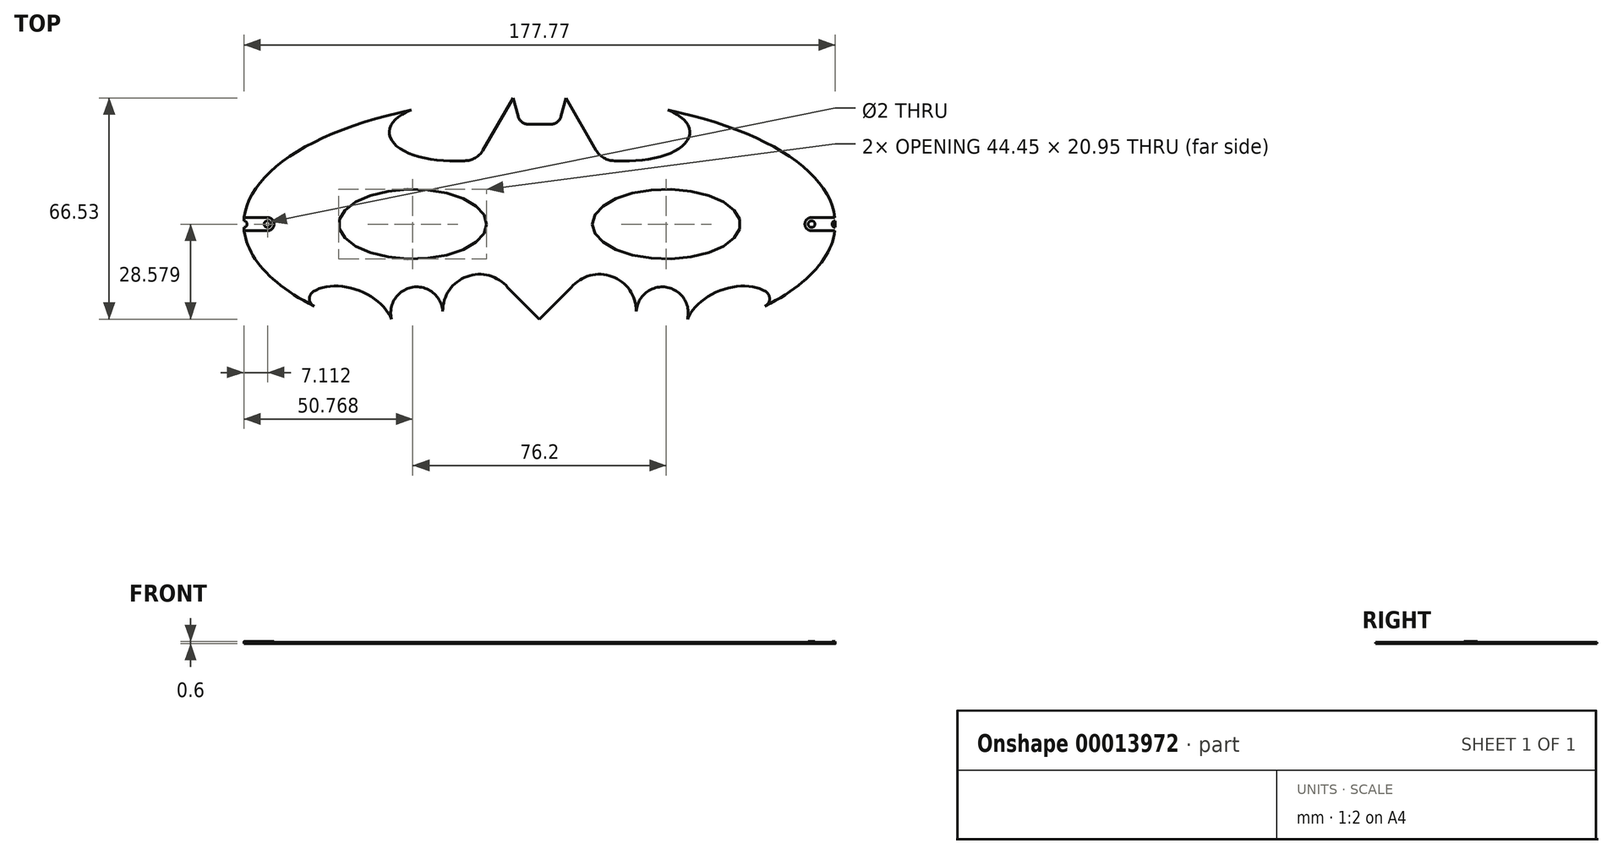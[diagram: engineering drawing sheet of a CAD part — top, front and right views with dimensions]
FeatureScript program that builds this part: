
annotation { "Feature Type Name" : "Feature", "Feature Type Description" : "" }
export const myFeature = defineFeature(function(context is Context, id is Id, definition is map)
    precondition{}
    {
        {
            var Q0;
            Q0=qCreatedBy(makeId("Top.planeOp"),FACE);
            var sketch = newSketch(context, id + "F0", { "sketchPlane" : qUnion([Q0])});
            skEllipse(sketch, "E0", {"center": v(-79.2, 13.69) * mm, "majorRadius": 22.23 * mm, "minorRadius": 10.48 * mm, "majorAxis": v(1, 0)});
            skLineSegment(sketch, "E1", {"start": v(-79.2, 13.69) * mm, "end": v(-41.1, 13.69) * mm, "construction": true});
            skLineSegment(sketch, "E2", {"start": v(-41.1, 13.69) * mm, "end": v(-41.1, 51.79) * mm, "construction": true});
            skLineSegment(sketch, "E3", {"start": v(-41.1, 13.69) * mm, "end": v(-41.1, -24.41) * mm, "construction": true});
            skEllipticalArc(sketch, "E4", {});
            skLineSegment(sketch, "E5", {"start": v(-63.62, 32.74) * mm, "end": v(-68.09, 32.74) * mm});
            skLineSegment(sketch, "E6", {"start": v(-44.49, 43.73) * mm, "end": v(-41.1, 43.73) * mm});
            skLineSegment(sketch, "E7", {"start": v(-41.1, 13.69) * mm, "end": v(-56.98, 13.69) * mm, "construction": true});
            skLineSegment(sketch, "E8", {"start": v(-49.04, 13.69) * mm, "end": v(-49.04, 51.64) * mm, "construction": true});
            skLineSegment(sketch, "E9", {"start": v(-49.04, 51.64) * mm, "end": v(-47.55, 46.09) * mm});
            skArc(sketch, "E10.filletArc", {"start": v(-47.55, 46.09) * mm, "mid": v(-46.42, 44.39) * mm, "end": v(-44.49, 43.73) * mm});
            skLineSegment(sketch, "E11", {"start": v(-49.04, 51.64) * mm, "end": v(-58.12, 35.91) * mm});
            skPoint(sketch, "E12.newPointA", {"position": v(-41.1, 32.74) * mm});
            skArc(sketch, "E12.filletArc", {"start": v(-63.62, 32.74) * mm, "mid": v(-60.44, 33.6) * mm, "end": v(-58.12, 35.91) * mm});
            skLineSegment(sketch, "E13", {"start": v(-56.98, 13.69) * mm, "end": v(-79.2, 13.69) * mm, "construction": true});
            skLineSegment(sketch, "E14", {"start": v(-68.09, 13.69) * mm, "end": v(-68.09, 50) * mm, "construction": true});
            skLineSegment(sketch, "E15", {"start": v(-68.09, 32.74) * mm, "end": v(-68.09, 50) * mm, "construction": true});
            skEllipticalArc(sketch, "E16", {});
            skLineSegment(sketch, "E17", {"start": v(-41.1, 43.73) * mm, "end": v(-41.1, -24.41) * mm, "construction": true});
            skPoint(sketch, "E18.orphan", {"position": v(-3, 13.69) * mm});
            skLineSegment(sketch, "E19", {"start": v(-41.1, 13.69) * mm, "end": v(-41.1, -14.89) * mm, "construction": true});
            skLineSegment(sketch, "E20", {"start": v(-41.1, -5.36) * mm, "end": v(-118.1, -5.36) * mm, "construction": true});
            skLineSegment(sketch, "E21", {"start": v(-41.1, -24.41) * mm, "end": v(-41.1, -5.36) * mm, "construction": true});
            skLineSegment(sketch, "E22", {"start": v(-79.2, 13.69) * mm, "end": v(-79.2, -20.73) * mm, "construction": true});
            skLineSegment(sketch, "E23", {"start": v(-79.2, -5.36) * mm, "end": v(-79.2, -20.73) * mm, "construction": true});
            skLineSegment(sketch, "E24", {"start": v(-79.2, -5.36) * mm, "end": v(-118.1, -5.36) * mm, "construction": true});
            skLineSegment(sketch, "E25", {"start": v(-98.65, -5.36) * mm, "end": v(-98.65, -15.35) * mm, "construction": true});
            skLineSegment(sketch, "E26", {"start": v(-79.2, -5.36) * mm, "end": v(-41.1, -5.36) * mm, "construction": true});
            skLineSegment(sketch, "E27", {"start": v(-60.15, -5.36) * mm, "end": v(-60.15, -23.53) * mm, "construction": true});
            skPoint(sketch, "E28.start.orphan", {"position": v(-41.1, -14.89) * mm});
            skLineSegment(sketch, "E29", {"start": v(-85.57, -14.89) * mm, "end": v(-85.61, -14.89) * mm});
            skPoint(sketch, "E30.orphan", {"position": v(-98.65, -14.89) * mm});
            skPoint(sketch, "E31.third.point", {"position": v(-101.98, -9.03) * mm});
            skLineSegment(sketch, "E32", {"start": v(-41.1, -14.89) * mm, "end": v(-50.63, -5.36) * mm});
            skArc(sketch, "E33", {"start": v(-50.63, -5.36) * mm, "mid": v(-62.9, -2.07) * mm, "end": v(-70.2, -12.49) * mm});
            skPoint(sketch, "E33.third.point", {"position": v(-69.11, -17.28) * mm});
            skLineSegment(sketch, "E34", {"start": v(-59.11, -12.49) * mm, "end": v(-70.2, -12.49) * mm, "construction": true});
            skArc(sketch, "E35", {"start": v(-70.2, -12.49) * mm, "mid": v(-79.46, -5.34) * mm, "end": v(-85.42, -15.4) * mm});
            skPoint(sketch, "E35.second.point", {"position": v(-85.57, -14.89) * mm});
            skPoint(sketch, "E35.third.point", {"position": v(-85.64, -14.58) * mm});
            skEllipticalArc(sketch, "E36", {});
            skArc(sketch, "E37.trimOffspring", {"start": v(-79.56, -20.66) * mm, "mid": v(-79.38, -20.7) * mm, "end": v(-79.2, -20.73) * mm});
            skEllipticalArc(sketch, "E38.trimOffspring", {});
            skArc(sketch, "E39", {"start": v(-109.08, -6.6) * mm, "mid": v(-110.26, -8.84) * mm, "end": v(-108.88, -10.97) * mm});
            skPoint(sketch, "E39.first.point", {"position": v(-109.08, -6.6) * mm});
            skPoint(sketch, "E39.second.point", {"position": v(-108.88, -10.97) * mm});
            skPoint(sketch, "E39.third.point", {"position": v(-105.79, -10.3) * mm});
            skEllipticalArc(sketch, "E40.0.MirrorCS", {});
            skArc(sketch, "E40.1.MirrorCS", {"start": v(-2.64, -20.66) * mm, "mid": v(-2.82, -20.7) * mm, "end": v(-3, -20.73) * mm});
            skArc(sketch, "E40.2.MirrorCS", {"start": v(-34.65, 46.09) * mm, "mid": v(-35.79, 44.39) * mm, "end": v(-37.72, 43.73) * mm});
            skLineSegment(sketch, "E40.3.MirrorCS", {"start": v(-37.72, 43.73) * mm, "end": v(-41.1, 43.73) * mm});
            skLineSegment(sketch, "E40.5.MirrorCS", {"start": v(-3, -5.36) * mm, "end": v(35.89, -5.36) * mm, "construction": true});
            skLineSegment(sketch, "E40.6.MirrorCS", {"start": v(-3, 13.69) * mm, "end": v(-41.1, 13.69) * mm, "construction": true});
            skLineSegment(sketch, "E40.7.MirrorCS", {"start": v(-3, -5.36) * mm, "end": v(-3, -20.73) * mm, "construction": true});
            skLineSegment(sketch, "E40.10.MirrorCS", {"start": v(-23.09, -12.49) * mm, "end": v(-12, -12.49) * mm, "construction": true});
            skPoint(sketch, "E40.11.MirrorP", {"position": v(-13.1, -17.28) * mm});
            skArc(sketch, "E40.12.MirrorCS", {"start": v(-31.58, -5.36) * mm, "mid": v(-19.3, -2.07) * mm, "end": v(-12, -12.49) * mm});
            skLineSegment(sketch, "E40.13.MirrorCS", {"start": v(-41.1, -5.36) * mm, "end": v(35.89, -5.36) * mm, "construction": true});
            skPoint(sketch, "E40.14.MirrorP", {"position": v(3.37, -14.89) * mm});
            skPoint(sketch, "E40.15.MirrorP", {"position": v(3.44, -14.58) * mm});
            skLineSegment(sketch, "E40.16.MirrorCS", {"start": v(-41.1, -14.89) * mm, "end": v(-31.58, -5.36) * mm});
            skEllipticalArc(sketch, "E40.17.MirrorCS", {});
            skEllipticalArc(sketch, "E40.18.MirrorCS", {});
            skLineSegment(sketch, "E40.20.MirrorCS", {"start": v(-3, -5.36) * mm, "end": v(-41.1, -5.36) * mm, "construction": true});
            skPoint(sketch, "E40.21.MirrorP", {"position": v(26.67, -10.97) * mm});
            skLineSegment(sketch, "E40.23.MirrorCS", {"start": v(-33.16, 51.64) * mm, "end": v(-24.09, 35.91) * mm});
            skArc(sketch, "E40.25.MirrorCS", {"start": v(26.88, -6.6) * mm, "mid": v(28.05, -8.84) * mm, "end": v(26.67, -10.97) * mm});
            skLineSegment(sketch, "E40.26.MirrorCS", {"start": v(-33.16, 13.69) * mm, "end": v(-33.16, 51.64) * mm, "construction": true});
            skPoint(sketch, "E40.27.MirrorP", {"position": v(23.58, -10.3) * mm});
            skLineSegment(sketch, "E40.28.MirrorCS", {"start": v(-3, 13.69) * mm, "end": v(-3, -20.73) * mm, "construction": true});
            skArc(sketch, "E40.29.MirrorCS", {"start": v(-18.59, 32.74) * mm, "mid": v(-21.76, 33.6) * mm, "end": v(-24.09, 35.91) * mm});
            skPoint(sketch, "E40.30.MirrorP", {"position": v(16.44, -14.89) * mm});
            skLineSegment(sketch, "E40.31.MirrorCS", {"start": v(-18.59, 32.74) * mm, "end": v(-14.11, 32.74) * mm});
            skLineSegment(sketch, "E40.32.MirrorCS", {"start": v(-14.11, 13.69) * mm, "end": v(-14.11, 50) * mm, "construction": true});
            skPoint(sketch, "E40.33.MirrorP", {"position": v(26.88, -6.6) * mm});
            skLineSegment(sketch, "E40.34.MirrorCS", {"start": v(-22.05, -5.36) * mm, "end": v(-22.05, -23.53) * mm, "construction": true});
            skLineSegment(sketch, "E40.35.MirrorCS", {"start": v(-41.1, 13.69) * mm, "end": v(-25.23, 13.69) * mm, "construction": true});
            skLineSegment(sketch, "E40.36.MirrorCS", {"start": v(-25.23, 13.69) * mm, "end": v(-3, 13.69) * mm, "construction": true});
            skPoint(sketch, "E40.37.MirrorP", {"position": v(19.77, -9.03) * mm});
            skLineSegment(sketch, "E40.38.MirrorCS", {"start": v(16.44, -5.36) * mm, "end": v(16.44, -15.35) * mm, "construction": true});
            skEllipse(sketch, "E40.39.MirrorC", {"center": v(-3, 13.69) * mm, "majorRadius": 22.23 * mm, "minorRadius": 10.48 * mm, "majorAxis": v(-1, 0)});
            skLineSegment(sketch, "E40.40.MirrorCS", {"start": v(-14.11, 32.74) * mm, "end": v(-14.11, 50) * mm, "construction": true});
            skLineSegment(sketch, "E40.41.MirrorCS", {"start": v(-33.16, 51.64) * mm, "end": v(-34.65, 46.09) * mm});
            skArc(sketch, "E40.42.MirrorCS", {"start": v(-12, -12.49) * mm, "mid": v(-2.74, -5.34) * mm, "end": v(3.22, -15.4) * mm});
            skEllipticalArc(sketch, "E40.43.MirrorCS", {});
            skEllipse(sketch, "E41.39.MirrorC", {"center": v(-3, 13.69) * mm, "majorRadius": 22.23 * mm, "minorRadius": 10.48 * mm, "majorAxis": v(-1, 0)});
            skEllipse(sketch, "E42.39.MirrorC", {"center": v(-3, 13.69) * mm, "majorRadius": 22.23 * mm, "minorRadius": 10.48 * mm, "majorAxis": v(-1, 0)});
            skLineSegment(sketch, "E43.2.MirrorCS", {"start": v(3.37, -14.89) * mm, "end": v(3.4, -14.89) * mm});
            skEllipse(sketch, "E43.40.MirrorC", {"center": v(-3, 13.69) * mm, "majorRadius": 22.23 * mm, "minorRadius": 10.48 * mm, "majorAxis": v(-1, 0)});
            const initialGuessF0  = {"E4": [-0.04110175946389499, 0.013689403422176838, -1, 0, 0.0889, 0.0381, 5.161492964245287, 0.7038030939227414], "E16": [-0.068089259463895, 0.041365408846871524, -1, 0, 0.018210322861197562, 0.008626005424694693, 5.403646126768505, 1.5707963267948966], "E36": [-0.0986465886621133, -0.014885596577823165, -0.9340282281485562, 0.35719920075732065, 0.014136312485541013, 0.009166058700018152, 3.6220749591931227, 5.829835207342765], "E38.trimOffspring": [-0.04110175946389499, 0.013689403422176838, -1, 0, 0.0889, 0.0381, 1.1233638688153285, 1.127885282721257], "E40.0.MirrorCS": [-0.04110175946389499, 0.013689403422176838, 1, 0, 0.0889, 0.0381, 5.155300024458329, 5.159821438364258], "E40.17.MirrorCS": [-0.04110175946389499, 0.013689403422176838, 1, 0, 0.0889, 0.0381, 5.579382213256845, 1.121692342934299], "E40.18.MirrorCS": [0.016443069734323315, -0.014885596577823165, 0.9340282281485562, 0.35719920075732065, 0.014136312485541013, 0.009166058700018152, 0.45335009983682095, 2.6611103479864635], "E40.43.MirrorCS": [-0.014114259463894982, 0.041365408846871524, 1, 0, 0.018210322861197562, 0.008626005424694693, 4.71238898038469, 0.879539180411081], "E40.0.MirrorCS": [-0.04110175946389499, 0.013689403422176838, 1, 0, 0.0889, 0.0381, 5.155300024458329, 5.159821438364258], "E40.17.MirrorCS": [-0.04110175946389499, 0.013689403422176838, 1, 0, 0.0889, 0.0381, 5.579382213256845, 1.121692342934299], "E40.18.MirrorCS": [0.016443069734323315, -0.014885596577823165, 0.9340282281485562, 0.35719920075732065, 0.014136312485541013, 0.009166058700018152, 0.45335009983682095, 2.6611103479864635], "E40.43.MirrorCS": [-0.014114259463894982, 0.041365408846871524, 1, 0, 0.018210322861197562, 0.008626005424694693, 4.71238898038469, 0.879539180411081], "E40.0.MirrorCS": [-0.04110175946389499, 0.013689403422176838, 1, 0, 0.0889, 0.0381, 5.155300024458329, 5.159821438364258], "E40.17.MirrorCS": [-0.04110175946389499, 0.013689403422176838, 1, 0, 0.0889, 0.0381, 5.579382213256845, 1.121692342934299], "E40.18.MirrorCS": [0.016443069734323315, -0.014885596577823165, 0.9340282281485562, 0.35719920075732065, 0.014136312485541013, 0.009166058700018152, 0.45335009983682095, 2.6611103479864635], "E40.43.MirrorCS": [-0.014114259463894982, 0.041365408846871524, 1, 0, 0.018210322861197562, 0.008626005424694693, 4.71238898038469, 0.879539180411081], "E40.43.MirrorCS": [-0.014114259463894982, 0.041365408846871524, 1, 0, 0.018210322861197562, 0.008626005424694693, 4.71238898038469, 0.879539180411081], "E40.17.MirrorCS": [-0.04110175946389499, 0.013689403422176838, 1, 0, 0.0889, 0.0381, 5.579382213256845, 1.121692342934299], "E40.0.MirrorCS": [-0.04110175946389499, 0.013689403422176838, 1, 0, 0.0889, 0.0381, 5.155300024458329, 5.159821438364258], "E40.17.MirrorCS": [-0.04110175946389499, 0.013689403422176838, 1, 0, 0.0889, 0.0381, 5.579382213256845, 1.121692342934299], "E40.18.MirrorCS": [0.016443069734323315, -0.014885596577823165, 0.9340282281485562, 0.35719920075732065, 0.014136312485541013, 0.009166058700018152, 0.45335009983682095, 2.6611103479864635], "E40.43.MirrorCS": [-0.014114259463894982, 0.041365408846871524, 1, 0, 0.018210322861197562, 0.008626005424694693, 4.71238898038469, 0.879539180411081]};
            skSetInitialGuess(sketch, initialGuessF0);
            skSolve(sketch);
        }
        {
            var Q0;
            Q0=makeQuery(id+"F0.imprint","IMPRINT",FACE,{"disambiguationData":[TD([[makeQuery(id+"F0.imprint","IMPRINT",EDGE,{"derivedFrom":sQuery(id+"F0.wireOp",EDGE,"E0")}),-1.0]])]});
            extrude(context, id + "F1", {"entities" : qUnion([Q0]), "depth" : .36 * mm});
        }
        {
            var Q0;
            Q0=makeQuery(id+"F1.opExtrude","CAP_FACE",FACE,{"disambiguationData":[OSD([sQuery(id+"F0.wireOp",EDGE,"E0"),sQuery(id+"F0.wireOp",EDGE,"E4"),sQuery(id+"F0.wireOp",EDGE,"E5"),sQuery(id+"F0.wireOp",EDGE,"E6"),sQuery(id+"F0.wireOp",EDGE,"E9"),sQuery(id+"F0.wireOp",EDGE,"E10.filletArc"),sQuery(id+"F0.wireOp",EDGE,"E11"),sQuery(id+"F0.wireOp",EDGE,"E12.filletArc"),sQuery(id+"F0.wireOp",EDGE,"E16"),sQuery(id+"F0.wireOp",EDGE,"E29"),sQuery(id+"F0.wireOp",EDGE,"E32"),sQuery(id+"F0.wireOp",EDGE,"E33"),sQuery(id+"F0.wireOp",EDGE,"E35"),sQuery(id+"F0.wireOp",EDGE,"E36"),sQuery(id+"F0.wireOp",EDGE,"E39"),sQuery(id+"F0.wireOp",EDGE,"E43.2.MirrorCS"),sQuery(id+"F0.wireOp",EDGE,"E40.3.MirrorCS"),sQuery(id+"F0.wireOp",EDGE,"E40.12.MirrorCS"),sQuery(id+"F0.wireOp",EDGE,"E40.16.MirrorCS"),sQuery(id+"F0.wireOp",EDGE,"E40.17.MirrorCS"),sQuery(id+"F0.wireOp",EDGE,"E40.2.MirrorCS"),sQuery(id+"F0.wireOp",EDGE,"E40.18.MirrorCS"),sQuery(id+"F0.wireOp",EDGE,"E40.23.MirrorCS"),sQuery(id+"F0.wireOp",EDGE,"E40.25.MirrorCS"),sQuery(id+"F0.wireOp",EDGE,"E40.29.MirrorCS"),sQuery(id+"F0.wireOp",EDGE,"E40.31.MirrorCS"),sQuery(id+"F0.wireOp",EDGE,"E43.40.MirrorC"),sQuery(id+"F0.wireOp",EDGE,"E40.41.MirrorCS"),sQuery(id+"F0.wireOp",EDGE,"E40.42.MirrorCS"),sQuery(id+"F0.wireOp",EDGE,"E40.43.MirrorCS")])],"isStart":false});
            var sketch = newSketch(context, id + "F2", { "sketchPlane" : qUnion([Q0])});
            skLineSegment(sketch, "E44.0", {"start": v(-37.72, 43.73) * mm, "end": v(-44.49, 43.73) * mm});
            skPoint(sketch, "E45.0", {"position": v(-41.1, -14.89) * mm});
            skLineSegment(sketch, "E46", {"start": v(-41.1, 43.73) * mm, "end": v(-41.1, -14.89) * mm, "construction": true});
            skLineSegment(sketch, "E47", {"start": v(-130, 13.69) * mm, "end": v(47.8, 13.69) * mm, "construction": true});
            skLineSegment(sketch, "E48", {"start": v(-130, 13.69) * mm, "end": v(-101.43, 13.69) * mm, "construction": true});
            skLineSegment(sketch, "E49", {"start": v(19.22, 13.69) * mm, "end": v(47.8, 13.69) * mm, "construction": true});
            skLineSegment(sketch, "E50", {"start": v(-115.71, 13.69) * mm, "end": v(33.51, 13.69) * mm, "construction": true});
            skLineSegment(sketch, "E51", {"start": v(-130, 13.69) * mm, "end": v(-115.71, 13.69) * mm, "construction": true});
            skCircle(sketch, "E52", {"center": v(-122.86, 13.69) * mm, "radius": 1 * mm});
            skArc(sketch, "E53", {"start": v(-122.98, 11.7) * mm, "mid": v(-120.86, 13.63) * mm, "end": v(-122.86, 15.69) * mm});
            skArc(sketch, "E54", {"start": v(-129.97, 12.69) * mm, "mid": v(-129, 13.69) * mm, "end": v(-129.97, 14.69) * mm});
            skEllipticalArc(sketch, "E55.0", {});
            skEllipticalArc(sketch, "E56.trimOffspring", {});
            skLineSegment(sketch, "E57", {"start": v(-129.88, 15.69) * mm, "end": v(-122.86, 15.69) * mm});
            skLineSegment(sketch, "E58", {"start": v(-129.88, 11.7) * mm, "end": v(-122.98, 11.7) * mm});
            skArc(sketch, "E59.0.MirrorCS", {"start": v(47.77, 12.69) * mm, "mid": v(46.8, 13.69) * mm, "end": v(47.77, 14.69) * mm});
            skLineSegment(sketch, "E60.0.MirrorCS", {"start": v(47.68, 15.69) * mm, "end": v(40.66, 15.69) * mm});
            skLineSegment(sketch, "E61.0.MirrorCS", {"start": v(47.68, 11.7) * mm, "end": v(40.78, 11.7) * mm});
            skArc(sketch, "E62.0.MirrorCS", {"start": v(40.78, 11.7) * mm, "mid": v(38.66, 13.63) * mm, "end": v(40.66, 15.69) * mm});
            skCircle(sketch, "E63.0.MirrorC", {"center": v(40.65, 13.69) * mm, "radius": 1 * mm});
            const initialGuessF2  = {"E55.0": [-0.04110175946389499, 0.013689403422176838, -1, 0, 0.0889, 0.0381, 5.161492964245287, 6.256947867074684], "E56.trimOffspring": [-0.04110175946389499, 0.013689403422176838, -1, 0, 0.0889, 0.0381, 0.026237440104901658, 0.7038030939227413]};
            skSetInitialGuess(sketch, initialGuessF2);
            skSolve(sketch);
        }
        {
            var Q0;
            Q0 = qSketchRegion(id + "F2", true);
            var Q1;
            {var subQ2=sQuery(id+"F2.wireOp",EDGE,"232e3cb7-d0a6-4b3f-8d78-17949714a0a3.0.MirrorCS");Q1=makeQuery(id+"F2.imprint","IMPRINT",FACE,{"disambiguationData":[TD([[makeQuery(id+"F2.imprint","IMPRINT",EDGE,{"derivedFrom":subQ2}),-1.0]])]});}
            var Q2;
            {var subQ2=sQuery(id+"F2.wireOp",EDGE,"E59.0.MirrorCS");Q2=makeQuery(id+"F2.imprint","IMPRINT",FACE,{"disambiguationData":[TD([[makeQuery(id+"F2.imprint","IMPRINT",EDGE,{"derivedFrom":subQ2}),1.0]])]});}
            extrude(context, id + "F3", {"entities" : qUnion([Q0, Q1, Q2]), "operationType" : NewBodyOperationType.ADD, "depth" : .24 * mm});
        }
        {
            var Q0;
            Q0=makeQuery(id+"F2.imprint","IMPRINT",FACE,{"disambiguationData":[TD([[makeQuery(id+"F2.imprint","IMPRINT",EDGE,{"derivedFrom":sQuery(id+"F2.wireOp",EDGE,"6cab86a7-9082-43a6-a316-eb2f96427bf0.0.MirrorC")}),-1.0]])]});
            var Q1;
            Q1=makeQuery(id+"F2.imprint","IMPRINT",FACE,{"disambiguationData":[TD([[makeQuery(id+"F2.imprint","IMPRINT",EDGE,{"derivedFrom":sQuery(id+"F2.wireOp",EDGE,"E52")}),1.0]])]});
            var Q2;
            {var subQ1=sQuery(id+"F2.wireOp",EDGE,"E54");Q2=makeQuery(id+"F2.imprint","IMPRINT",FACE,{"disambiguationData":[TD([[makeQuery(id+"F2.imprint","IMPRINT",EDGE,{"derivedFrom":subQ1}),1.0]])]});}
            var Q3;
            {var subQ1=sQuery(id+"F2.wireOp",EDGE,"80558438-93c2-4d96-bbcd-f9e5bd7c3d5a.0.MirrorCS");Q3=makeQuery(id+"F2.imprint","IMPRINT",FACE,{"disambiguationData":[TD([[makeQuery(id+"F2.imprint","IMPRINT",EDGE,{"derivedFrom":subQ1}),-1.0]])]});}
            var Q4;
            {var subQ1=sQuery(id+"F2.wireOp",EDGE,"E59.0.MirrorCS");Q4=makeQuery(id+"F2.imprint","IMPRINT",FACE,{"disambiguationData":[TD([[makeQuery(id+"F2.imprint","IMPRINT",EDGE,{"derivedFrom":subQ1}),-1.0]])]});}
            var Q5;
            Q5=makeQuery(id+"F2.imprint","IMPRINT",FACE,{"disambiguationData":[TD([[makeQuery(id+"F2.imprint","IMPRINT",EDGE,{"derivedFrom":sQuery(id+"F2.wireOp",EDGE,"E63.0.MirrorC")}),-1.0]])]});
            extrude(context, id + "F4", {"entities" : qUnion([Q0, Q1, Q2, Q3, Q4, Q5]), "operationType" : NewBodyOperationType.REMOVE, "endBound" : BoundingType.THROUGH_ALL, "oppositeDirection" : true, "depth" : 25.4 * mm, "hasSecondDirection" : true, "secondDirectionBound" : SecondDirectionBoundingType.THROUGH_ALL, "secondDirectionOppositeDirection" : false, "secondDirectionDepth" : 25.4 * mm});
        }
    });
